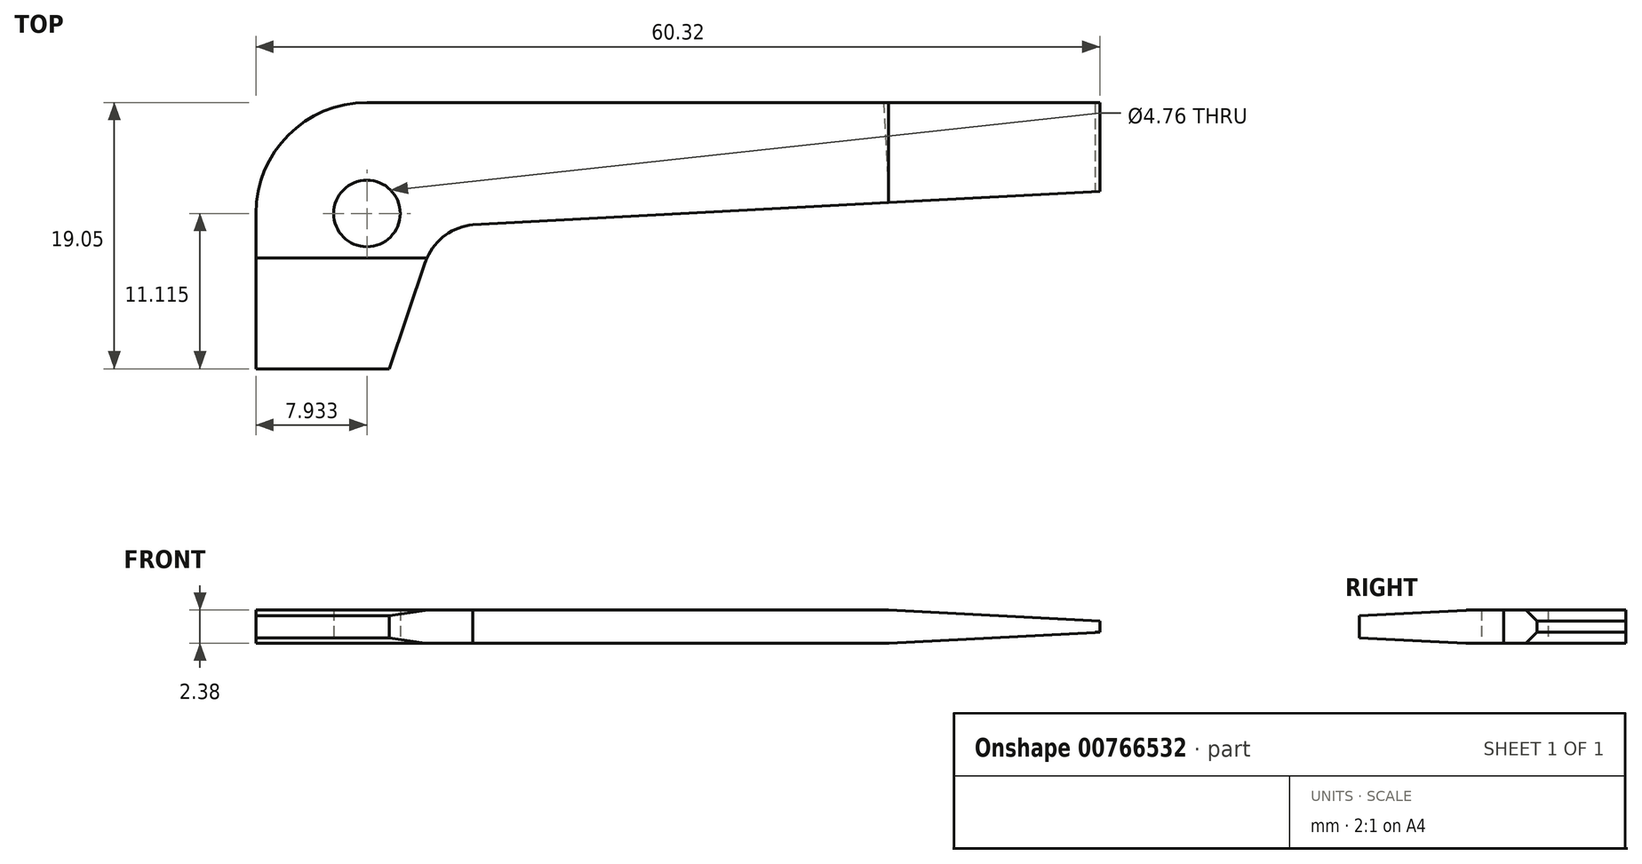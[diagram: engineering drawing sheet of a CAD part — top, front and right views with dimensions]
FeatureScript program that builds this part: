
annotation { "Feature Type Name" : "Feature", "Feature Type Description" : "" }
export const myFeature = defineFeature(function(context is Context, id is Id, definition is map)
    precondition{}
    {
        {
            var Q0;
            Q0=qCreatedBy(makeId("Top.planeOp"),FACE);
            var sketch = newSketch(context, id + "F0", { "sketchPlane" : qUnion([Q0])});
            skLineSegment(sketch, "E0", {"start": v(-53.44, 46.44) * mm, "end": v(6.88, 46.44) * mm});
            skLineSegment(sketch, "E1", {"start": v(-53.44, 46.44) * mm, "end": v(-53.44, 27.4) * mm});
            skLineSegment(sketch, "E2", {"start": v(-53.44, 27.4) * mm, "end": v(-43.92, 27.4) * mm});
            skLineSegment(sketch, "E3", {"start": v(6.88, 46.44) * mm, "end": v(6.88, 40.1) * mm});
            skArc(sketch, "E4", {"start": v(-37.92, 37.7) * mm, "mid": v(-40.02, 36.86) * mm, "end": v(-41.33, 35.02) * mm});
            skLineSegment(sketch, "E5", {"start": v(-43.92, 27.4) * mm, "end": v(-41.33, 35.02) * mm});
            skCircle(sketch, "E6", {"center": v(-45.5, 38.5) * mm, "radius": 2.38 * mm});
            skLineSegment(sketch, "E7", {"start": v(6.88, 40.1) * mm, "end": v(-37.92, 37.7) * mm});
            skSolve(sketch);
        }
        {
            var Q0;
            Q0=makeQuery(id+"F0.imprint","IMPRINT",FACE,{"disambiguationData":[TD([[makeQuery(id+"F0.imprint","IMPRINT",EDGE,{"derivedFrom":sQuery(id+"F0.wireOp",EDGE,"E0")}),-1.0]])]});
            extrude(context, id + "F1", {"entities" : qUnion([Q0]), "depth" : 2.38 * mm, "offsetDistance" : 25.4 * mm});
        }
        {
            var Q0;
            Q0=makeQuery(id+"F1.opExtrude","SWEPT_EDGE",EDGE,{"disambiguationData":[OSD([sQuery(id+"F0.wireOp",EDGE,"E0"),sQuery(id+"F0.wireOp",EDGE,"E1")])]});
            fillet(context, id + "F2", {"entities" : qUnion([Q0]), "radius" : 7.94 * mm, "tangentPropagation" : true, "allowEdgeOverflow" : false});
        }
        {
            var Q0;
            Q0=makeQuery(id+"F1.opExtrude","SWEPT_FACE",FACE,{"disambiguationData":[OSD([sQuery(id+"F0.wireOp",EDGE,"E0")])]});
            var sketch = newSketch(context, id + "F3", { "sketchPlane" : qUnion([Q0])});
            skLineSegment(sketch, "E8", {"start": v(-6.88, 1.6) * mm, "end": v(8.22, 2.38) * mm});
            skLineSegment(sketch, "E9", {"start": v(8.22, 2.38) * mm, "end": v(8.2, 2.73) * mm});
            skLineSegment(sketch, "E10", {"start": v(8.2, 2.73) * mm, "end": v(-7.22, 3.2) * mm});
            skLineSegment(sketch, "E11", {"start": v(-7.22, 3.2) * mm, "end": v(-7.27, 1.55) * mm});
            skLineSegment(sketch, "E12", {"start": v(-7.27, 1.55) * mm, "end": v(-6.88, 1.6) * mm});
            skSolve(sketch);
        }
        {
            var Q0;
            Q0 = qSketchRegion(id + "F3", true);
            extrude(context, id + "F4", {"entities" : qUnion([Q0]), "operationType" : NewBodyOperationType.REMOVE, "endBound" : BoundingType.THROUGH_ALL, "oppositeDirection" : true, "depth" : 25.4 * mm, "offsetDistance" : 25.4 * mm});
        }
        {
            var Q0;
            Q0=makeQuery(id+"F1.opExtrude","SWEPT_FACE",FACE,{"disambiguationData":[OSD([sQuery(id+"F0.wireOp",EDGE,"E7")])]});
            var sketch = newSketch(context, id + "F5", { "sketchPlane" : qUnion([Q0])});
            skLineSegment(sketch, "E13", {"start": v(-6.08, 0) * mm, "end": v(9.01, 0.8) * mm});
            skLineSegment(sketch, "E14", {"start": v(9.01, 0.8) * mm, "end": v(9.01, 0) * mm});
            skLineSegment(sketch, "E15", {"start": v(9.01, 0) * mm, "end": v(-6.08, 0) * mm});
            skLineSegment(sketch, "E16", {"start": v(-6.08, 0) * mm, "end": v(-6.08, 0) * mm});
            skSolve(sketch);
        }
        {
            var Q0;
            Q0 = qSketchRegion(id + "F5", true);
            extrude(context, id + "F6", {"entities" : qUnion([Q0]), "operationType" : NewBodyOperationType.REMOVE, "endBound" : BoundingType.THROUGH_ALL, "oppositeDirection" : true, "depth" : 25.4 * mm, "offsetDistance" : 25.4 * mm});
        }
        {
            var Q0;
            Q0=makeQuery(id+"F1.opExtrude","SWEPT_FACE",FACE,{"disambiguationData":[OSD([sQuery(id+"F0.wireOp",EDGE,"E0")])]});
            var sketch = newSketch(context, id + "F7", { "sketchPlane" : qUnion([Q0])});
            skLineSegment(sketch, "E17", {"start": v(-6.88, 0.8) * mm, "end": v(-6.54, 0.8) * mm});
            skLineSegment(sketch, "E18", {"start": v(-6.54, 0.8) * mm, "end": v(-6.54, -0.1) * mm});
            skLineSegment(sketch, "E19", {"start": v(-6.54, -0.1) * mm, "end": v(-6.98, -0.1) * mm});
            skLineSegment(sketch, "E20", {"start": v(-6.98, -0.1) * mm, "end": v(-6.98, 0.8) * mm});
            skLineSegment(sketch, "E21", {"start": v(-6.98, 0.8) * mm, "end": v(-6.88, 0.8) * mm});
            skSolve(sketch);
        }
        {
            var Q0;
            Q0 = qSketchRegion(id + "F7", true);
            extrude(context, id + "F8", {"entities" : qUnion([Q0]), "operationType" : NewBodyOperationType.REMOVE, "endBound" : BoundingType.THROUGH_ALL, "oppositeDirection" : true, "depth" : 25.4 * mm, "offsetDistance" : 25.4 * mm});
        }
        {
            var Q0;
            Q0=makeQuery(id+"F1.opExtrude","SWEPT_FACE",FACE,{"disambiguationData":[OSD([sQuery(id+"F0.wireOp",EDGE,"E1")])]});
            var sketch = newSketch(context, id + "F9", { "sketchPlane" : qUnion([Q0])});
            skPoint(sketch, "E22", {"position": v(-27.4, 1.98) * mm});
            skPoint(sketch, "E23", {"position": v(-27.4, 0.4) * mm});
            skPoint(sketch, "E24", {"position": v(-35.33, 2.38) * mm});
            skPoint(sketch, "E25", {"position": v(-35.34, 0) * mm});
            skLineSegment(sketch, "E26", {"start": v(-27.4, 1.98) * mm, "end": v(-35.33, 2.38) * mm});
            skLineSegment(sketch, "E27", {"start": v(-35.33, 2.38) * mm, "end": v(-26.71, 2.73) * mm});
            skLineSegment(sketch, "E28", {"start": v(-26.71, 2.73) * mm, "end": v(-26.68, 1.98) * mm});
            skLineSegment(sketch, "E29", {"start": v(-26.68, 1.98) * mm, "end": v(-27.4, 1.98) * mm});
            skLineSegment(sketch, "E30", {"start": v(-27.4, 0.4) * mm, "end": v(-35.34, 0) * mm});
            skLineSegment(sketch, "E31", {"start": v(-35.34, 0) * mm, "end": v(-35.01, -0.3) * mm});
            skLineSegment(sketch, "E32", {"start": v(-35.01, -0.3) * mm, "end": v(-26.82, -0.3) * mm});
            skLineSegment(sketch, "E33", {"start": v(-26.82, -0.3) * mm, "end": v(-26.94, 0.4) * mm});
            skLineSegment(sketch, "E34", {"start": v(-26.94, 0.4) * mm, "end": v(-27.4, 0.4) * mm});
            skSolve(sketch);
        }
        {
            var Q0;
            Q0 = qSketchRegion(id + "F9", true);
            extrude(context, id + "F10", {"entities" : qUnion([Q0]), "operationType" : NewBodyOperationType.REMOVE, "endBound" : BoundingType.THROUGH_ALL, "oppositeDirection" : true, "depth" : 25.4 * mm, "offsetDistance" : 25.4 * mm});
        }
    });
